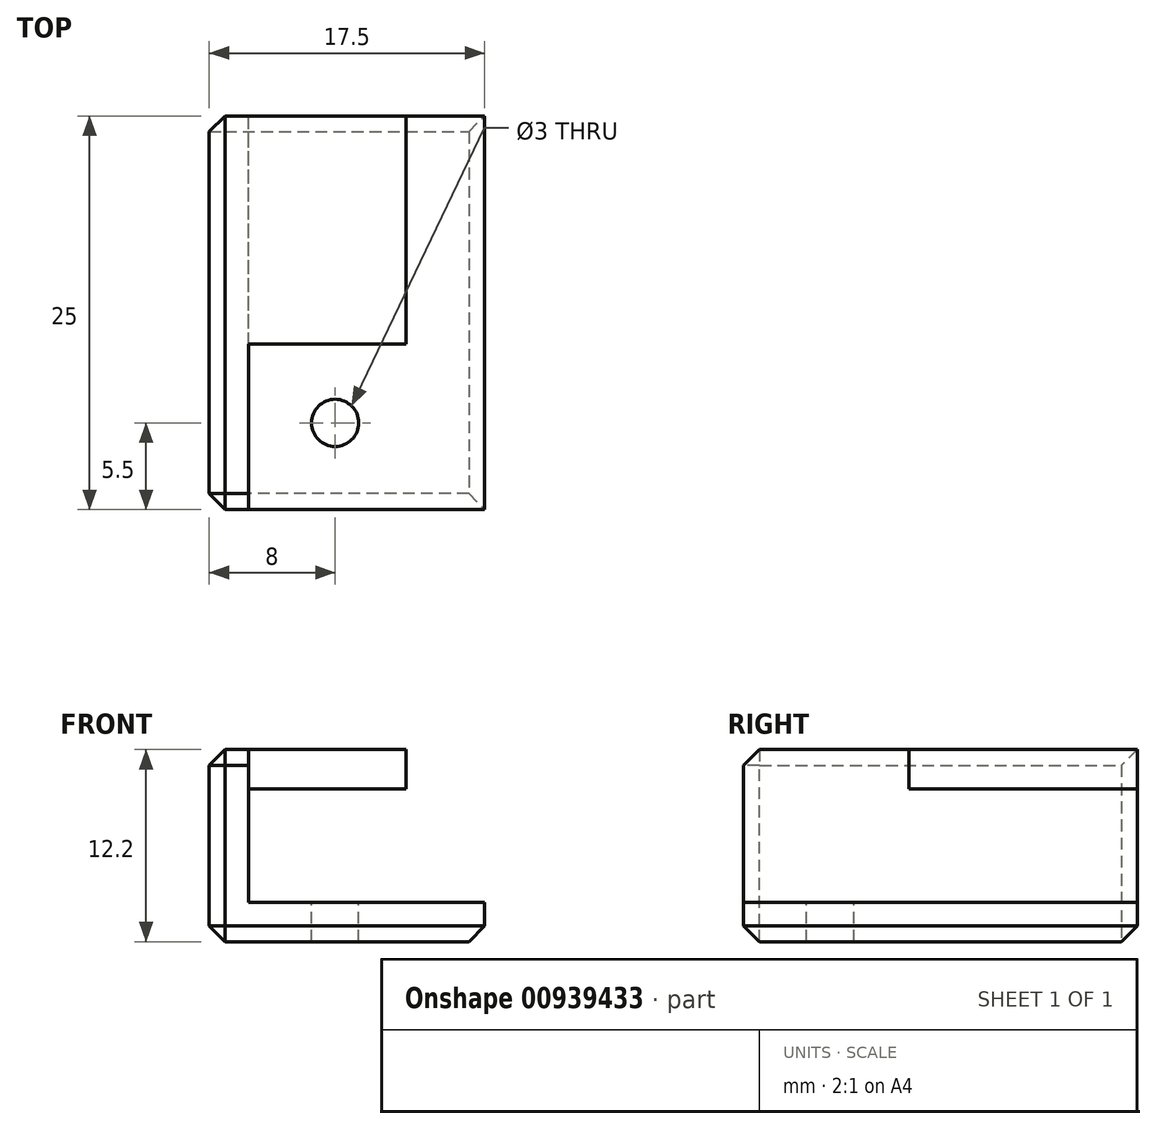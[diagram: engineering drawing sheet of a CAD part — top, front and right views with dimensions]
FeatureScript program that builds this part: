
annotation { "Feature Type Name" : "Feature", "Feature Type Description" : "" }
export const myFeature = defineFeature(function(context is Context, id is Id, definition is map)
    precondition{}
    {
        {
            var Q0;
            Q0=qCreatedBy(makeId("Front.planeOp"),FACE);
            var sketch = newSketch(context, id + "F0", { "sketchPlane" : qUnion([Q0])});
            skLineSegment(sketch, "E0", {"start": v(0, 3.6) * mm, "end": v(0, -3.6) * mm});
            skLineSegment(sketch, "E1", {"start": v(0, -3.6) * mm, "end": v(15, -3.6) * mm});
            skLineSegment(sketch, "E2", {"start": v(0, 3.6) * mm, "end": v(10, 3.6) * mm});
            skLineSegment(sketch, "E3.0", {"start": v(-2.5, -6.1) * mm, "end": v(15, -6.1) * mm});
            skLineSegment(sketch, "E3.1", {"start": v(-2.5, 6.1) * mm, "end": v(-2.5, -6.1) * mm});
            skLineSegment(sketch, "E3.2", {"start": v(-2.5, 6.1) * mm, "end": v(10, 6.1) * mm});
            skLineSegment(sketch, "E4", {"start": v(10, 6.1) * mm, "end": v(10, 3.6) * mm});
            skLineSegment(sketch, "E5", {"start": v(15, -3.6) * mm, "end": v(15, -6.1) * mm});
            skSolve(sketch);
        }
        {
            var Q0;
            Q0=qSketchRegion(id+"F0",true);
            extrude(context, id + "F1", {"entities" : qUnion([Q0]), "depth" : 25 * mm, "offsetDistance" : 25 * mm});
        }
        {
            var Q0;
            Q0=makeQuery(id+"F1.opExtrude","SWEPT_FACE",FACE,{"disambiguationData":[OSD([sQuery(id+"F0.wireOp",EDGE,"E3.2")])]});
            var sketch = newSketch(context, id + "F2", { "sketchPlane" : qUnion([Q0])});
            skCircle(sketch, "E6", {"center": v(5.5, -19.5) * mm, "radius": 1.5 * mm});
            skSolve(sketch);
        }
        {
            var Q0;
            Q0=makeQuery(id+"F2.imprint","IMPRINT",FACE,{"disambiguationData":[TD([[makeQuery(id+"F2.imprint","IMPRINT",EDGE,{"derivedFrom":sQuery(id+"F2.wireOp",EDGE,"E6")}),1.0]])]});
            var Q1;
            Q1=sQuery(id+"F2.wireOp",EDGE,"E6");
            extrude(context, id + "F3", {"entities" : qUnion([Q0]), "operationType" : NewBodyOperationType.REMOVE, "surfaceEntities" : qUnion([Q1]), "oppositeDirection" : true, "depth" : 25 * mm, "offsetDistance" : 25 * mm});
        }
        {
            var Q0;
            Q0=makeQuery(id+"F1.opExtrude","SWEPT_FACE",FACE,{"disambiguationData":[OSD([sQuery(id+"F0.wireOp",EDGE,"E3.2")])]});
            var sketch = newSketch(context, id + "F4", { "sketchPlane" : qUnion([Q0])});
            skLineSegment(sketch, "E7", {"start": v(0, -25) * mm, "end": v(0, -14.5) * mm});
            skLineSegment(sketch, "E8", {"start": v(0, -14.5) * mm, "end": v(10, -14.5) * mm});
            skSolve(sketch);
        }
        {
            var Q0;
            {var subQ5=sQuery(id+"F4.wireOp",EDGE,"E7");Q0=makeQuery(id+"F4.imprint","IMPRINT",FACE,{"disambiguationData":[TD([[makeQuery(id+"F4.imprint","IMPRINT",EDGE,{"derivedFrom":subQ5}),-1.0]])]});}
            extrude(context, id + "F5", {"entities" : qUnion([Q0]), "operationType" : NewBodyOperationType.REMOVE, "oppositeDirection" : true, "depth" : 5 * mm, "offsetDistance" : 25 * mm});
        }
        {
            var Q0;
            Q0=makeQuery(id+"F1.opExtrude","SWEPT_EDGE",EDGE,{"disambiguationData":[OSD([sQuery(id+"F0.wireOp",EDGE,"E3.0"),sQuery(id+"F0.wireOp",EDGE,"E5")])]});
            var Q1;
            Q1=makeQuery(id+"F1.opExtrude","CAP_EDGE",EDGE,{"disambiguationData":[OSD([sQuery(id+"F0.wireOp",EDGE,"E3.0")])],"isStart":true});
            var Q2;
            Q2=makeQuery(id+"F1.opExtrude","CAP_EDGE",EDGE,{"disambiguationData":[OSD([sQuery(id+"F0.wireOp",EDGE,"E3.0")])],"isStart":false});
            var Q3;
            Q3=makeQuery(id+"F1.opExtrude","SWEPT_EDGE",EDGE,{"disambiguationData":[OSD([sQuery(id+"F0.wireOp",EDGE,"E3.1"),sQuery(id+"F0.wireOp",EDGE,"E3.2")])]});
            var Q4;
            Q4=makeQuery(id+"F1.opExtrude","CAP_EDGE",EDGE,{"disambiguationData":[OSD([sQuery(id+"F0.wireOp",EDGE,"E3.2")])],"isStart":false});
            var Q5;
            Q5=makeQuery(id+"F1.opExtrude","CAP_EDGE",EDGE,{"disambiguationData":[OSD([sQuery(id+"F0.wireOp",EDGE,"E3.1")])],"isStart":false});
            var Q6;
            Q6=makeQuery(id+"F1.opExtrude","CAP_EDGE",EDGE,{"disambiguationData":[OSD([sQuery(id+"F0.wireOp",EDGE,"E3.1")])],"isStart":true});
            var Q7;
            Q7=makeQuery(id+"F1.opExtrude","SWEPT_EDGE",EDGE,{"disambiguationData":[OSD([sQuery(id+"F0.wireOp",EDGE,"E3.0"),sQuery(id+"F0.wireOp",EDGE,"E3.1")])]});
            chamfer(context, id + "F6", {"entities" : qUnion([Q0, Q1, Q2, Q3, Q4, Q5, Q6, Q7]), "width" : 1 * mm, "tangentPropagation" : true});
        }
    });
